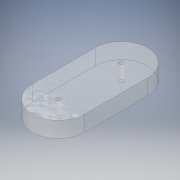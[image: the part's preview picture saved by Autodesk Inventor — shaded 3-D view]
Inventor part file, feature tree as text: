
AUTODESK INVENTOR PART (.ipt)
format: ipt  version: 2019 (Build 230136000, 136)  size: 126,464 bytes
history: native  units: mm
features: extrude x1, sketch x1
ambient origin geometry x8: Origin, YZ Plane, XZ Plane, XY Plane, X Axis, Y Axis, Z Axis, Center Point
bodies: Solid1 (feature_tree)
feature tree (2):
  extrude  "Extrusion1"  Depth=20.0mm
  sketch  "Sketch1"  dims[d15=6.0mm d16=0.0mm d25=13.0mm d26=14.0mm d30=5.0mm d31=5.0mm d32=1.8mm d33=20.0mm]
